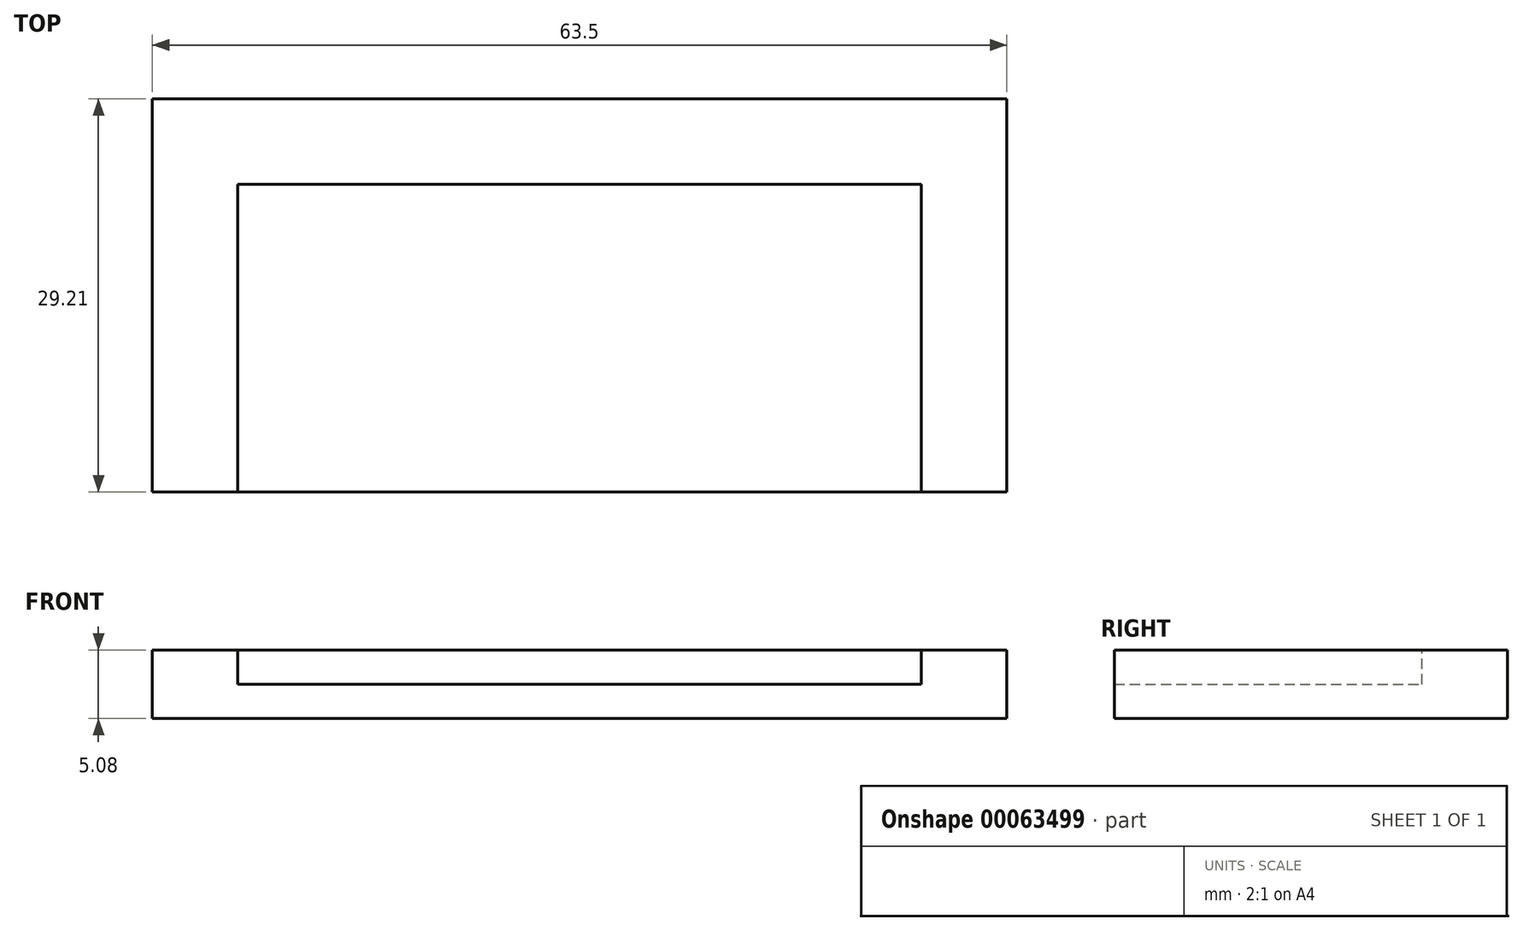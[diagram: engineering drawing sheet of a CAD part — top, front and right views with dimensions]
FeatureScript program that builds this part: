
annotation { "Feature Type Name" : "Feature", "Feature Type Description" : "" }
export const myFeature = defineFeature(function(context is Context, id is Id, definition is map)
    precondition{}
    {
        {
            var Q0;
            Q0=qCreatedBy(makeId("Top.planeOp"),FACE);
            var sketch = newSketch(context, id + "F0", { "sketchPlane" : qUnion([Q0])});
            skLineSegment(sketch, "E0.bottom", {"start": v(0, 0) * mm, "end": v(63.5, 0) * mm});
            skLineSegment(sketch, "E0.top", {"start": v(0, 31.75) * mm, "end": v(63.5, 31.75) * mm});
            skLineSegment(sketch, "E0.left", {"start": v(0, 0) * mm, "end": v(0, 31.75) * mm});
            skLineSegment(sketch, "E0.right", {"start": v(63.5, 0) * mm, "end": v(63.5, 31.75) * mm});
            skSolve(sketch);
        }
        {
            var Q0;
            Q0 = qSketchRegion(id + "F0", true);
            extrude(context, id + "F1", {"entities" : qUnion([Q0]), "depth" : 5.08 * mm});
        }
        {
            var Q0;
            Q0=makeQuery(id+"F1.opExtrude","CAP_FACE",FACE,{"disambiguationData":[OSD([sQuery(id+"F0.wireOp",EDGE,"E0.bottom"),sQuery(id+"F0.wireOp",EDGE,"E0.top"),sQuery(id+"F0.wireOp",EDGE,"E0.left"),sQuery(id+"F0.wireOp",EDGE,"E0.right")])],"isStart":false});
            var sketch = newSketch(context, id + "F2", { "sketchPlane" : qUnion([Q0])});
            skLineSegment(sketch, "E1.bottom", {"start": v(57.15, 0) * mm, "end": v(6.35, 0) * mm});
            skLineSegment(sketch, "E1.top", {"start": v(57.15, 25.4) * mm, "end": v(6.35, 25.4) * mm});
            skLineSegment(sketch, "E1.left", {"start": v(57.15, 0) * mm, "end": v(57.15, 25.4) * mm});
            skLineSegment(sketch, "E1.right", {"start": v(6.35, 0) * mm, "end": v(6.35, 25.4) * mm});
            skSolve(sketch);
        }
        {
            var Q0;
            Q0 = qSketchRegion(id + "F2", true);
            extrude(context, id + "F3", {"entities" : qUnion([Q0]), "operationType" : NewBodyOperationType.REMOVE, "oppositeDirection" : true, "depth" : 2.54 * mm});
        }
        {
            var Q0;
            Q0=makeQuery(id+"F1.opExtrude","CAP_FACE",FACE,{"disambiguationData":[OSD([sQuery(id+"F0.wireOp",EDGE,"E0.bottom"),sQuery(id+"F0.wireOp",EDGE,"E0.top"),sQuery(id+"F0.wireOp",EDGE,"E0.left"),sQuery(id+"F0.wireOp",EDGE,"E0.right")])],"isStart":false});
            var sketch = newSketch(context, id + "F4", { "sketchPlane" : qUnion([Q0])});
            skLineSegment(sketch, "E2.bottom", {"start": v(63.5, 0) * mm, "end": v(0, 0) * mm});
            skLineSegment(sketch, "E2.top", {"start": v(63.5, 2.54) * mm, "end": v(0, 2.54) * mm});
            skLineSegment(sketch, "E2.left", {"start": v(63.5, 0) * mm, "end": v(63.5, 2.54) * mm});
            skLineSegment(sketch, "E2.right", {"start": v(0, 0) * mm, "end": v(0, 2.54) * mm});
            skSolve(sketch);
        }
        {
            var Q0;
            Q0 = qSketchRegion(id + "F4", true);
            extrude(context, id + "F5", {"entities" : qUnion([Q0]), "operationType" : NewBodyOperationType.REMOVE, "oppositeDirection" : true, "depth" : 25.4 * mm});
        }
    });
